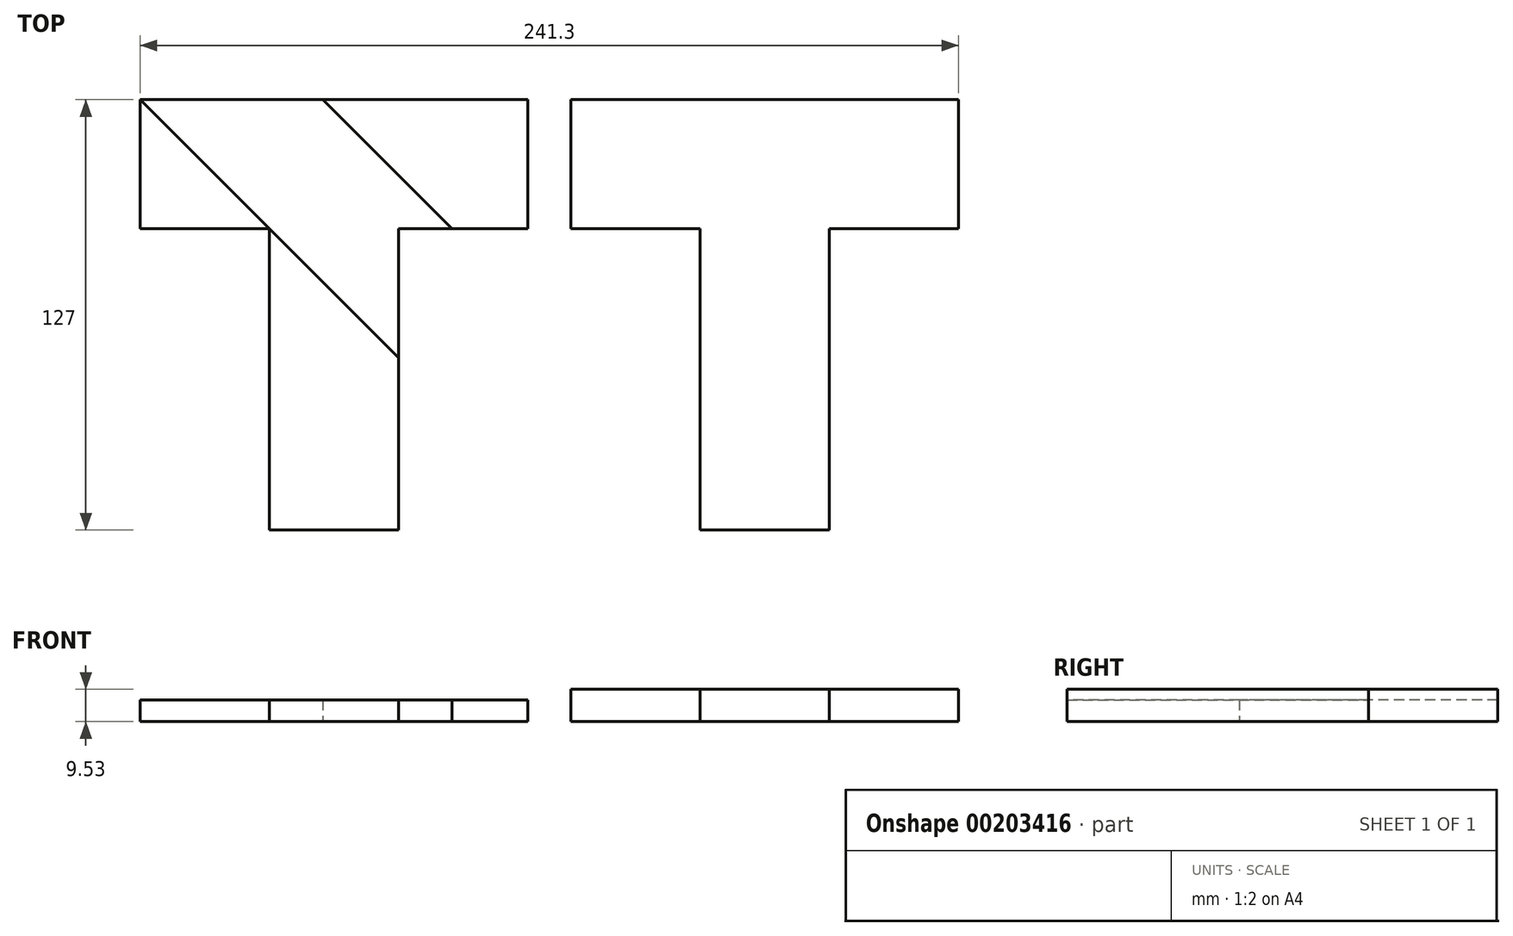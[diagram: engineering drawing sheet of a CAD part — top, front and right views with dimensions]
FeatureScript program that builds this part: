
annotation { "Feature Type Name" : "Feature", "Feature Type Description" : "" }
export const myFeature = defineFeature(function(context is Context, id is Id, definition is map)
    precondition{}
    {
        {
            var Q0;
            Q0=qCreatedBy(makeId("Top.planeOp"),FACE);
            var sketch = newSketch(context, id + "F0", { "sketchPlane" : qUnion([Q0])});
            skLineSegment(sketch, "E0", {"start": v(23.64, -60.75) * mm, "end": v(-14.46, -60.75) * mm});
            skLineSegment(sketch, "E1", {"start": v(-14.46, -60.75) * mm, "end": v(-14.46, 28.15) * mm});
            skLineSegment(sketch, "E2", {"start": v(-14.46, 28.15) * mm, "end": v(-52.56, 28.15) * mm});
            skLineSegment(sketch, "E3", {"start": v(-52.56, 28.15) * mm, "end": v(-52.56, 66.25) * mm});
            skLineSegment(sketch, "E4", {"start": v(-52.56, 66.25) * mm, "end": v(61.74, 66.25) * mm});
            skLineSegment(sketch, "E5", {"start": v(61.74, 66.25) * mm, "end": v(61.74, 28.15) * mm});
            skLineSegment(sketch, "E6", {"start": v(61.74, 28.15) * mm, "end": v(23.64, 28.15) * mm});
            skLineSegment(sketch, "E7", {"start": v(23.64, 28.15) * mm, "end": v(23.64, -60.75) * mm});
            skLineSegment(sketch, "E8", {"start": v(-52.56, 66.25) * mm, "end": v(23.64, -9.95) * mm});
            skLineSegment(sketch, "E9", {"start": v(1.32, 66.25) * mm, "end": v(39.42, 28.15) * mm});
            skLineSegment(sketch, "E10", {"start": v(-17.25, 30.94) * mm, "end": v(9.69, 57.88) * mm, "construction": true});
            skSolve(sketch);
        }
        {
            var Q0;
            {var subQ0=sQuery(id+"F0.wireOp",EDGE,"E2");Q0=makeQuery(id+"F0.imprint","IMPRINT",FACE,{"disambiguationData":[TD([[makeQuery(id+"F0.imprint","IMPRINT",EDGE,{"derivedFrom":subQ0}),-1.0]])]});}
            extrude(context, id + "F1", {"entities" : qUnion([Q0]), "depth" : 6.35 * mm});
        }
        {
            var Q0;
            {var subQ8=sQuery(id+"F0.wireOp",EDGE,"E9");Q0=makeQuery(id+"F0.imprint","IMPRINT",FACE,{"disambiguationData":[TD([[makeQuery(id+"F0.imprint","IMPRINT",EDGE,{"derivedFrom":subQ8}),-1.0]])]});}
            extrude(context, id + "F2", {"entities" : qUnion([Q0]), "depth" : 6.35 * mm});
        }
        {
            var Q0;
            {var subQ0=sQuery(id+"F0.wireOp",EDGE,"E5");Q0=makeQuery(id+"F0.imprint","IMPRINT",FACE,{"disambiguationData":[TD([[makeQuery(id+"F0.imprint","IMPRINT",EDGE,{"derivedFrom":subQ0}),-1.0]])]});}
            extrude(context, id + "F3", {"entities" : qUnion([Q0]), "depth" : 6.35 * mm});
        }
        {
            var Q0;
            {var subQ0=sQuery(id+"F0.wireOp",EDGE,"E0");Q0=makeQuery(id+"F0.imprint","IMPRINT",FACE,{"disambiguationData":[TD([[makeQuery(id+"F0.imprint","IMPRINT",EDGE,{"derivedFrom":subQ0}),-1.0]])]});}
            extrude(context, id + "F4", {"entities" : qUnion([Q0]), "depth" : 6.35 * mm});
        }
        {
            var Q0;
            {var subQ0=sQuery(id+"F0.wireOp",EDGE,"E2");Q0=makeQuery(id+"F0.imprint","IMPRINT",FACE,{"disambiguationData":[TD([[makeQuery(id+"F0.imprint","IMPRINT",EDGE,{"derivedFrom":subQ0}),-1.0]])]});}
            var Q1;
            {var subQ0=sQuery(id+"F0.wireOp",EDGE,"E0");Q1=makeQuery(id+"F0.imprint","IMPRINT",FACE,{"disambiguationData":[TD([[makeQuery(id+"F0.imprint","IMPRINT",EDGE,{"derivedFrom":subQ0}),-1.0]])]});}
            var Q2;
            {var subQ8=sQuery(id+"F0.wireOp",EDGE,"E9");Q2=makeQuery(id+"F0.imprint","IMPRINT",FACE,{"disambiguationData":[TD([[makeQuery(id+"F0.imprint","IMPRINT",EDGE,{"derivedFrom":subQ8}),-1.0]])]});}
            var Q3;
            {var subQ0=sQuery(id+"F0.wireOp",EDGE,"E5");Q3=makeQuery(id+"F0.imprint","IMPRINT",FACE,{"disambiguationData":[TD([[makeQuery(id+"F0.imprint","IMPRINT",EDGE,{"derivedFrom":subQ0}),-1.0]])]});}
            extrude(context, id + "F5", {"entities" : qUnion([Q0, Q1, Q2, Q3]), "depth" : 9.52 * mm});
        }
        {
            var Q0;
            Q0=makeQuery(id+"F5.opExtrude","SWEPT_BODY",BODY,{"disambiguationData":[OSD([sQuery(id+"F0.wireOp",EDGE,"E0"),sQuery(id+"F0.wireOp",EDGE,"E1"),sQuery(id+"F0.wireOp",EDGE,"E2"),sQuery(id+"F0.wireOp",EDGE,"E3"),sQuery(id+"F0.wireOp",EDGE,"E4"),sQuery(id+"F0.wireOp",EDGE,"E5"),sQuery(id+"F0.wireOp",EDGE,"E6"),sQuery(id+"F0.wireOp",EDGE,"E7")])]});
            transform(context, id + "F6", {"entities" : qUnion([Q0]), "transformType" : TransformType.TRANSLATION_3D, "dx" : 127 * mm, "dy" : 0 * mm, "dz" : 0 * mm, "makeCopy" : false});
        }
    });
